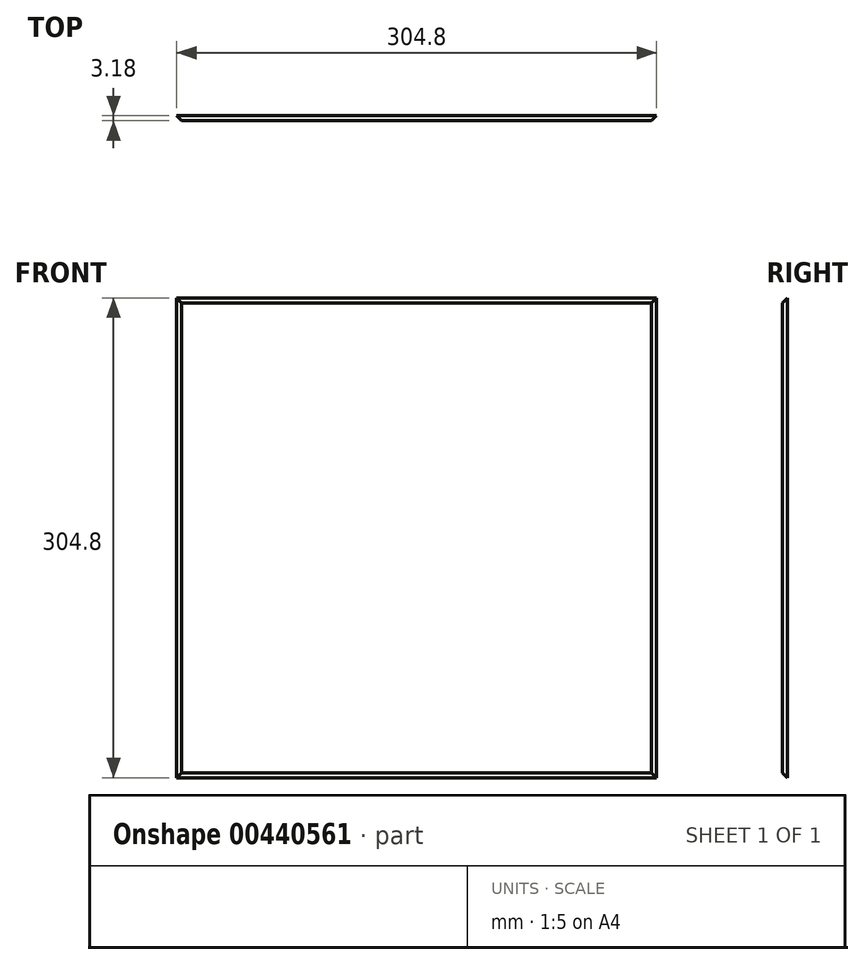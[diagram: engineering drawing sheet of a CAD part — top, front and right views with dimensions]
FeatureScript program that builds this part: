
annotation { "Feature Type Name" : "Feature", "Feature Type Description" : "" }
export const myFeature = defineFeature(function(context is Context, id is Id, definition is map)
    precondition{}
    {
        {
            var Q0;
            Q0=qCreatedBy(makeId("Front.planeOp"),FACE);
            var sketch = newSketch(context, id + "F0", { "sketchPlane" : qUnion([Q0])});
            skLineSegment(sketch, "E0.bottom", {"start": v(-152.4, 152.4) * mm, "end": v(152.4, 152.4) * mm});
            skLineSegment(sketch, "E0.top", {"start": v(-152.4, -152.4) * mm, "end": v(152.4, -152.4) * mm});
            skLineSegment(sketch, "E0.left", {"start": v(-152.4, 152.4) * mm, "end": v(-152.4, -152.4) * mm});
            skLineSegment(sketch, "E0.right", {"start": v(152.4, 152.4) * mm, "end": v(152.4, -152.4) * mm});
            skPoint(sketch, "E0.middle", {"position": v(0, 0) * mm});
            skSolve(sketch);
        }
        {
            var Q0;
            Q0=makeQuery(id+"F0.imprint","IMPRINT",FACE,{"disambiguationData":[TD([[makeQuery(id+"F0.imprint","IMPRINT",EDGE,{"derivedFrom":sQuery(id+"F0.wireOp",EDGE,"E0.bottom")}),-1.0]])]});
            cPlane(context, id + "F1", {"entities" : qUnion([Q0]), "cplaneType" : CPlaneType.OFFSET, "offset" : 3.17 * mm, "width" : 152.4 * mm, "height" : 152.4 * mm});
        }
        {
            var Q0;
            Q0=qCreatedBy(id+"F1.planeOp",FACE);
            var sketch = newSketch(context, id + "F2", { "sketchPlane" : qUnion([Q0])});
            skLineSegment(sketch, "E1.bottom", {"start": v(-149.22, 149.23) * mm, "end": v(149.23, 149.23) * mm});
            skLineSegment(sketch, "E1.top", {"start": v(-149.23, -149.23) * mm, "end": v(149.22, -149.23) * mm});
            skLineSegment(sketch, "E1.left", {"start": v(-149.22, 149.23) * mm, "end": v(-149.23, -149.22) * mm});
            skLineSegment(sketch, "E1.right", {"start": v(149.23, 149.23) * mm, "end": v(149.22, -149.22) * mm});
            skPoint(sketch, "E1.middle", {"position": v(0, 0) * mm});
            skSolve(sketch);
        }
        {
            var Q0;
            Q0=makeQuery(id+"F0.imprint","IMPRINT",FACE,{"disambiguationData":[TD([[makeQuery(id+"F0.imprint","IMPRINT",EDGE,{"derivedFrom":sQuery(id+"F0.wireOp",EDGE,"E0.bottom")}),-1.0]])]});
            var Q1;
            Q1=makeQuery(id+"F2.imprint","IMPRINT",FACE,{"disambiguationData":[TD([[makeQuery(id+"F2.imprint","IMPRINT",EDGE,{"derivedFrom":sQuery(id+"F2.wireOp",EDGE,"E1.bottom")}),-1.0]])]});
            loft(context, id + "F3", {"sheetProfilesArray" : [{ "sheetProfileEntities" : qUnion([Q0]) }, { "sheetProfileEntities" : qUnion([Q1]) }]});
        }
    });
